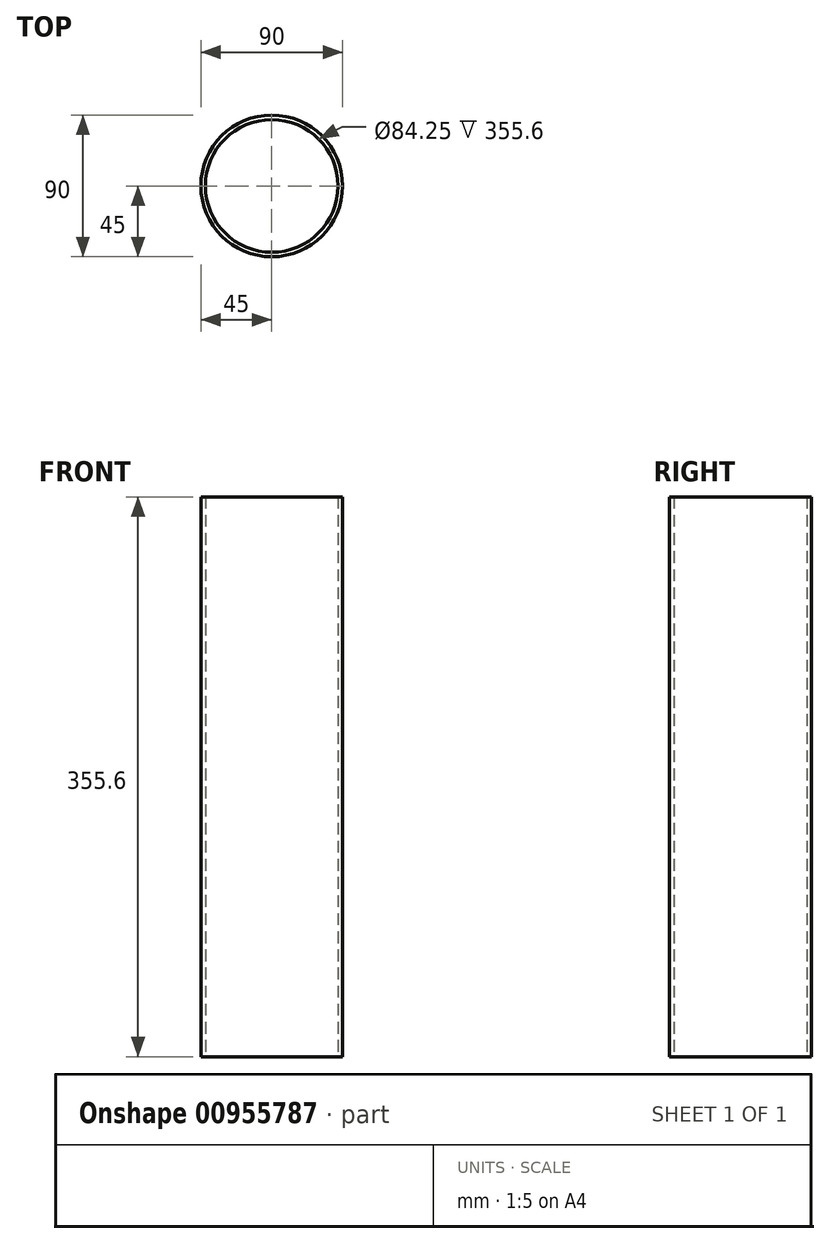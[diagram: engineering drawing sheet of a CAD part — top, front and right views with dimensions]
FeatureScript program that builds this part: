
annotation { "Feature Type Name" : "Feature", "Feature Type Description" : "" }
export const myFeature = defineFeature(function(context is Context, id is Id, definition is map)
    precondition{}
    {
        {
            var Q0;
            Q0=qCreatedBy(makeId("Top.planeOp"),FACE);
            var sketch = newSketch(context, id + "F0", { "sketchPlane" : qUnion([Q0])});
            skCircle(sketch, "E0", {"center": v(0, 0) * mm, "radius": 45 * mm});
            skCircle(sketch, "E1", {"center": v(0, 0) * mm, "radius": 42.12 * mm});
            skSolve(sketch);
        }
        {
            var Q0;
            Q0=makeQuery(id+"F0.imprint","IMPRINT",FACE,{"disambiguationData":[TD([[makeQuery(id+"F0.imprint","IMPRINT",EDGE,{"derivedFrom":sQuery(id+"F0.wireOp",EDGE,"E0")}),1.0]])]});
            extrude(context, id + "F1", {"entities" : qUnion([Q0]), "depth" : 355.6 * mm, "offsetDistance" : 25 * mm});
        }
    });
